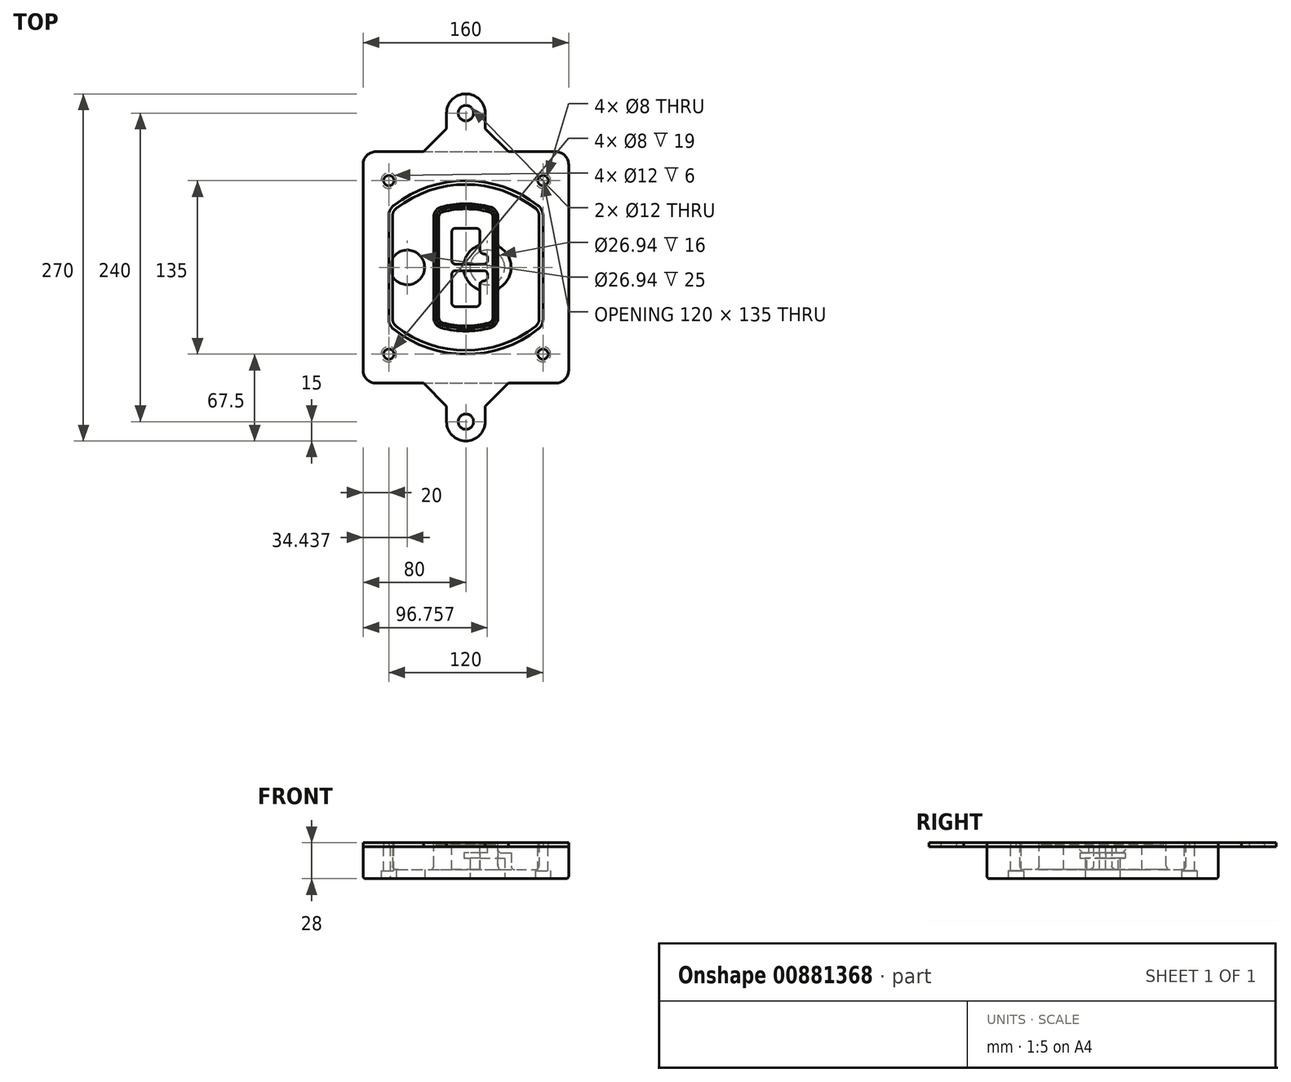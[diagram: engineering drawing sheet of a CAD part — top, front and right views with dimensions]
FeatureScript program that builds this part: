
annotation { "Feature Type Name" : "Feature", "Feature Type Description" : "" }
export const myFeature = defineFeature(function(context is Context, id is Id, definition is map)
    precondition{}
    {
        {
            var Q0;
            Q0=qCreatedBy(makeId("Top.planeOp"),FACE);
            var sketch = newSketch(context, id + "F0", { "sketchPlane" : qUnion([Q0])});
            skPoint(sketch, "E0.rect.middle", {"position": v(0, 0) * mm});
            skLineSegment(sketch, "E1.bottom", {"start": v(-70, -90) * mm, "end": v(70, -90) * mm});
            skLineSegment(sketch, "E1.top", {"start": v(-70, 90) * mm, "end": v(70, 90) * mm});
            skLineSegment(sketch, "E1.left", {"start": v(-80, -80) * mm, "end": v(-80, 80) * mm});
            skLineSegment(sketch, "E1.right", {"start": v(80, -80) * mm, "end": v(80, 80) * mm});
            skLineSegment(sketch, "E2", {"start": v(-80, 90) * mm, "end": v(80, -90) * mm, "construction": true});
            skLineSegment(sketch, "E3", {"start": v(80, 90) * mm, "end": v(-80, -90) * mm, "construction": true});
            skCircle(sketch, "E4", {"center": v(-60, 67.5) * mm, "radius": 4 * mm});
            skCircle(sketch, "E5", {"center": v(60, 67.5) * mm, "radius": 4 * mm});
            skCircle(sketch, "E6", {"center": v(60, -67.5) * mm, "radius": 4 * mm});
            skCircle(sketch, "E7", {"center": v(-60, -67.5) * mm, "radius": 4 * mm});
            skLineSegment(sketch, "E8", {"start": v(-60, 67.5) * mm, "end": v(60, 67.5) * mm, "construction": true});
            skLineSegment(sketch, "E9", {"start": v(60, 67.5) * mm, "end": v(60, -67.5) * mm, "construction": true});
            skLineSegment(sketch, "E10", {"start": v(60, -67.5) * mm, "end": v(-60, -67.5) * mm, "construction": true});
            skLineSegment(sketch, "E11", {"start": v(-60, -67.5) * mm, "end": v(-60, 67.5) * mm, "construction": true});
            skLineSegment(sketch, "E12", {"start": v(-60, 40.3) * mm, "end": v(-60, -40.3) * mm});
            skLineSegment(sketch, "E13", {"start": v(60, 40.3) * mm, "end": v(60, -40.3) * mm});
            skArc(sketch, "E14", {"start": v(56.15, 48.18) * mm, "mid": v(0, 67.5) * mm, "end": v(-56.15, 48.18) * mm});
            skArc(sketch, "E15", {"start": v(-56.15, -48.18) * mm, "mid": v(0, -67.5) * mm, "end": v(56.15, -48.18) * mm});
            skLineSegment(sketch, "E16", {"start": v(-60, 0) * mm, "end": v(60, 0) * mm, "construction": true});
            skPoint(sketch, "E17.visualSharp", {"position": v(-60, -45) * mm});
            skArc(sketch, "E17.filletArc", {"start": v(-60, -40.3) * mm, "mid": v(-58.99, -44.68) * mm, "end": v(-56.15, -48.18) * mm});
            skPoint(sketch, "E18.visualSharp", {"position": v(-60, 45) * mm});
            skArc(sketch, "E18.filletArc", {"start": v(-56.15, 48.18) * mm, "mid": v(-58.99, 44.68) * mm, "end": v(-60, 40.3) * mm});
            skPoint(sketch, "E19.visualSharp", {"position": v(60, 45) * mm});
            skArc(sketch, "E19.filletArc", {"start": v(60, 40.3) * mm, "mid": v(58.99, 44.68) * mm, "end": v(56.15, 48.18) * mm});
            skPoint(sketch, "E20.visualSharp", {"position": v(60, -45) * mm});
            skArc(sketch, "E20.filletArc", {"start": v(56.15, -48.18) * mm, "mid": v(58.99, -44.68) * mm, "end": v(60, -40.3) * mm});
            skPoint(sketch, "E21.visualSharp", {"position": v(-80, 90) * mm});
            skArc(sketch, "E21.filletArc", {"start": v(-70, 90) * mm, "mid": v(-77.07, 87.07) * mm, "end": v(-80, 80) * mm});
            skPoint(sketch, "E22.visualSharp", {"position": v(80, 90) * mm});
            skArc(sketch, "E22.filletArc", {"start": v(80, 80) * mm, "mid": v(77.07, 87.07) * mm, "end": v(70, 90) * mm});
            skPoint(sketch, "E23.visualSharp", {"position": v(80, -90) * mm});
            skArc(sketch, "E23.filletArc", {"start": v(70, -90) * mm, "mid": v(77.07, -87.07) * mm, "end": v(80, -80) * mm});
            skPoint(sketch, "E24.visualSharp", {"position": v(-80, -90) * mm});
            skArc(sketch, "E24.filletArc", {"start": v(-80, -80) * mm, "mid": v(-77.07, -87.07) * mm, "end": v(-70, -90) * mm});
            skArc(sketch, "E25.0", {"start": v(57, 40.3) * mm, "mid": v(56.3, 43.36) * mm, "end": v(54.3, 45.81) * mm});
            skLineSegment(sketch, "E25.1", {"start": v(57, 40.3) * mm, "end": v(57, -40.3) * mm});
            skArc(sketch, "E25.2", {"start": v(54.3, -45.81) * mm, "mid": v(56.3, -43.36) * mm, "end": v(57, -40.3) * mm});
            skArc(sketch, "E25.3", {"start": v(-54.3, -45.81) * mm, "mid": v(0, -64.5) * mm, "end": v(54.3, -45.81) * mm});
            skArc(sketch, "E25.4", {"start": v(-57, -40.3) * mm, "mid": v(-56.3, -43.36) * mm, "end": v(-54.3, -45.81) * mm});
            skArc(sketch, "E25.5", {"start": v(54.3, 45.81) * mm, "mid": v(0, 64.5) * mm, "end": v(-54.3, 45.81) * mm});
            skLineSegment(sketch, "E25.6", {"start": v(-57, 40.3) * mm, "end": v(-57, -40.3) * mm});
            skArc(sketch, "E25.7", {"start": v(-54.3, 45.81) * mm, "mid": v(-56.3, 43.36) * mm, "end": v(-57, 40.3) * mm});
            skArc(sketch, "E26.0", {"start": v(-58.62, 51.33) * mm, "mid": v(-62.58, 46.43) * mm, "end": v(-64, 40.3) * mm});
            skArc(sketch, "E26.1", {"start": v(58.62, 51.33) * mm, "mid": v(0, 71.5) * mm, "end": v(-58.62, 51.33) * mm});
            skArc(sketch, "E26.2", {"start": v(64, 40.3) * mm, "mid": v(62.58, 46.43) * mm, "end": v(58.62, 51.33) * mm});
            skLineSegment(sketch, "E26.3", {"start": v(64, 40.3) * mm, "end": v(64, -40.3) * mm});
            skArc(sketch, "E26.4", {"start": v(58.62, -51.33) * mm, "mid": v(62.58, -46.43) * mm, "end": v(64, -40.3) * mm});
            skLineSegment(sketch, "E26.5", {"start": v(-64, 40.3) * mm, "end": v(-64, -40.3) * mm});
            skArc(sketch, "E26.6", {"start": v(-58.62, -51.33) * mm, "mid": v(0, -71.5) * mm, "end": v(58.62, -51.33) * mm});
            skArc(sketch, "E26.7", {"start": v(-64, -40.3) * mm, "mid": v(-62.58, -46.43) * mm, "end": v(-58.62, -51.33) * mm});
            skSolve(sketch);
        }
        {
            var Q0;
            Q0=makeQuery(id+"F0.imprint","IMPRINT",FACE,{"disambiguationData":[TD([[makeQuery(id+"F0.imprint","IMPRINT",EDGE,{"derivedFrom":sQuery(id+"F0.wireOp",EDGE,"E1.bottom")}),1.0]])]});
            var Q1;
            Q1=makeQuery(id+"F0.imprint","IMPRINT",FACE,{"disambiguationData":[TD([[makeQuery(id+"F0.imprint","IMPRINT",EDGE,{"derivedFrom":sQuery(id+"F0.wireOp",EDGE,"E12")}),1.0]])]});
            var Q2;
            Q2=makeQuery(id+"F0.imprint","IMPRINT",FACE,{"disambiguationData":[TD([[makeQuery(id+"F0.imprint","IMPRINT",EDGE,{"derivedFrom":sQuery(id+"F0.wireOp",EDGE,"E25.0")}),1.0]])]});
            var Q3;
            Q3=makeQuery(id+"F0.imprint","IMPRINT",FACE,{"disambiguationData":[TD([[makeQuery(id+"F0.imprint","IMPRINT",EDGE,{"derivedFrom":sQuery(id+"F0.wireOp",EDGE,"E12")}),-1.0]])]});
            extrude(context, id + "F1", {"entities" : qUnion([Q0, Q1, Q2, Q3]), "oppositeDirection" : true, "depth" : 25 * mm});
        }
        {
            var Q0;
            Q0=makeQuery(id+"F0.imprint","IMPRINT",FACE,{"disambiguationData":[TD([[makeQuery(id+"F0.imprint","IMPRINT",EDGE,{"derivedFrom":sQuery(id+"F0.wireOp",EDGE,"E12")}),1.0]])]});
            extrude(context, id + "F2", {"entities" : qUnion([Q0]), "operationType" : NewBodyOperationType.ADD, "depth" : 3 * mm});
        }
        {
            var Q0;
            Q0=makeQuery(id+"F0.imprint","IMPRINT",FACE,{"disambiguationData":[TD([[makeQuery(id+"F0.imprint","IMPRINT",EDGE,{"derivedFrom":sQuery(id+"F0.wireOp",EDGE,"E25.0")}),1.0]])]});
            extrude(context, id + "F3", {"entities" : qUnion([Q0]), "operationType" : NewBodyOperationType.REMOVE, "oppositeDirection" : true, "depth" : 18 * mm});
        }
        {
            var Q0;
            Q0=makeQuery(id+"F2.opExtrude","CAP_FACE",FACE,{"disambiguationData":[OSD([sQuery(id+"F0.wireOp",EDGE,"E12"),sQuery(id+"F0.wireOp",EDGE,"E13"),sQuery(id+"F0.wireOp",EDGE,"E14"),sQuery(id+"F0.wireOp",EDGE,"E15"),sQuery(id+"F0.wireOp",EDGE,"E17.filletArc"),sQuery(id+"F0.wireOp",EDGE,"E18.filletArc"),sQuery(id+"F0.wireOp",EDGE,"E19.filletArc"),sQuery(id+"F0.wireOp",EDGE,"E20.filletArc"),sQuery(id+"F0.wireOp",EDGE,"E25.0"),sQuery(id+"F0.wireOp",EDGE,"E25.1"),sQuery(id+"F0.wireOp",EDGE,"E25.2"),sQuery(id+"F0.wireOp",EDGE,"E25.3"),sQuery(id+"F0.wireOp",EDGE,"E25.4"),sQuery(id+"F0.wireOp",EDGE,"E25.5"),sQuery(id+"F0.wireOp",EDGE,"E25.6"),sQuery(id+"F0.wireOp",EDGE,"E25.7")])],"isStart":false});
            var sketch = newSketch(context, id + "F4", { "sketchPlane" : qUnion([Q0])});
            skArc(sketch, "E27.0", {"start": v(-19.08, -46.97) * mm, "mid": v(0, -49.5) * mm, "end": v(19.08, -46.97) * mm});
            skArc(sketch, "E28.0", {"start": v(19.08, 46.97) * mm, "mid": v(0, 49.5) * mm, "end": v(-19.08, 46.97) * mm});
            skLineSegment(sketch, "E29", {"start": v(-25, 39.25) * mm, "end": v(-25, -39.25) * mm});
            skLineSegment(sketch, "E30", {"start": v(25, 39.25) * mm, "end": v(25, -39.25) * mm});
            skLineSegment(sketch, "E31", {"start": v(-25, 45.1) * mm, "end": v(25, 45.1) * mm, "construction": true});
            skLineSegment(sketch, "E32", {"start": v(-25, -45.1) * mm, "end": v(25, -45.1) * mm, "construction": true});
            skPoint(sketch, "E33.visualSharp", {"position": v(-25, 45.1) * mm});
            skArc(sketch, "E33.filletArc", {"start": v(-19.08, 46.97) * mm, "mid": v(-23.35, 44.11) * mm, "end": v(-25, 39.25) * mm});
            skPoint(sketch, "E34.visualSharp", {"position": v(25, 45.1) * mm});
            skArc(sketch, "E34.filletArc", {"start": v(25, 39.25) * mm, "mid": v(23.35, 44.11) * mm, "end": v(19.08, 46.97) * mm});
            skPoint(sketch, "E35.visualSharp", {"position": v(25, -45.1) * mm});
            skArc(sketch, "E35.filletArc", {"start": v(19.08, -46.97) * mm, "mid": v(23.35, -44.11) * mm, "end": v(25, -39.25) * mm});
            skPoint(sketch, "E36.visualSharp", {"position": v(-25, -45.1) * mm});
            skArc(sketch, "E36.filletArc", {"start": v(-25, -39.25) * mm, "mid": v(-23.35, -44.11) * mm, "end": v(-19.08, -46.97) * mm});
            skArc(sketch, "E37.0", {"start": v(54.3, 45.81) * mm, "mid": v(0, 64.5) * mm, "end": v(-54.3, 45.81) * mm});
            skArc(sketch, "E37.1", {"start": v(-54.3, 45.81) * mm, "mid": v(-56.3, 43.36) * mm, "end": v(-57, 40.3) * mm});
            skLineSegment(sketch, "E37.2", {"start": v(-57, 40.3) * mm, "end": v(-57, -40.3) * mm});
            skArc(sketch, "E37.3", {"start": v(-57, -40.3) * mm, "mid": v(-56.3, -43.36) * mm, "end": v(-54.3, -45.81) * mm});
            skArc(sketch, "E37.4", {"start": v(-54.3, -45.81) * mm, "mid": v(0, -64.5) * mm, "end": v(54.3, -45.81) * mm});
            skArc(sketch, "E37.5", {"start": v(54.3, -45.81) * mm, "mid": v(56.3, -43.36) * mm, "end": v(57, -40.3) * mm});
            skLineSegment(sketch, "E37.6", {"start": v(57, 40.3) * mm, "end": v(57, -40.3) * mm});
            skArc(sketch, "E37.7", {"start": v(57, 40.3) * mm, "mid": v(56.3, 43.36) * mm, "end": v(54.3, 45.81) * mm});
            skLineSegment(sketch, "E38.0", {"start": v(23, 39.25) * mm, "end": v(23, -39.25) * mm});
            skArc(sketch, "E38.1", {"start": v(18.56, -45.04) * mm, "mid": v(21.76, -42.9) * mm, "end": v(23, -39.25) * mm});
            skArc(sketch, "E38.2", {"start": v(-18.56, -45.04) * mm, "mid": v(0, -47.5) * mm, "end": v(18.56, -45.04) * mm});
            skArc(sketch, "E38.3", {"start": v(-23, -39.25) * mm, "mid": v(-21.76, -42.9) * mm, "end": v(-18.56, -45.04) * mm});
            skLineSegment(sketch, "E38.4", {"start": v(-23, 39.25) * mm, "end": v(-23, -39.25) * mm});
            skArc(sketch, "E38.5", {"start": v(23, 39.25) * mm, "mid": v(21.76, 42.9) * mm, "end": v(18.56, 45.04) * mm});
            skArc(sketch, "E38.6", {"start": v(-18.56, 45.04) * mm, "mid": v(-21.76, 42.9) * mm, "end": v(-23, 39.25) * mm});
            skArc(sketch, "E38.7", {"start": v(18.56, 45.04) * mm, "mid": v(0, 47.5) * mm, "end": v(-18.56, 45.04) * mm});
            skArc(sketch, "E39.0", {"start": v(21, 39.25) * mm, "mid": v(20.18, 41.68) * mm, "end": v(18.04, 43.1) * mm});
            skLineSegment(sketch, "E39.1", {"start": v(21, 39.25) * mm, "end": v(21, -39.25) * mm});
            skArc(sketch, "E39.2", {"start": v(18.04, -43.1) * mm, "mid": v(20.18, -41.68) * mm, "end": v(21, -39.25) * mm});
            skArc(sketch, "E39.3", {"start": v(-18.04, -43.1) * mm, "mid": v(0, -45.5) * mm, "end": v(18.04, -43.1) * mm});
            skArc(sketch, "E39.4", {"start": v(-21, -39.25) * mm, "mid": v(-20.18, -41.68) * mm, "end": v(-18.04, -43.1) * mm});
            skArc(sketch, "E39.5", {"start": v(18.04, 43.1) * mm, "mid": v(0, 45.5) * mm, "end": v(-18.04, 43.1) * mm});
            skLineSegment(sketch, "E39.6", {"start": v(-21, 39.25) * mm, "end": v(-21, -39.25) * mm});
            skArc(sketch, "E39.7", {"start": v(-18.04, 43.1) * mm, "mid": v(-20.18, 41.68) * mm, "end": v(-21, 39.25) * mm});
            skLineSegment(sketch, "E40", {"start": v(-25, 0) * mm, "end": v(25, 0) * mm, "construction": true});
            skLineSegment(sketch, "E41", {"start": v(-11, 5.5) * mm, "end": v(-11, 27.5) * mm});
            skLineSegment(sketch, "E42", {"start": v(-8, 30.5) * mm, "end": v(8, 30.5) * mm});
            skLineSegment(sketch, "E43", {"start": v(11, 27.5) * mm, "end": v(11, 13.5) * mm});
            skLineSegment(sketch, "E44", {"start": v(14, 10.5) * mm, "end": v(14, 10.5) * mm});
            skLineSegment(sketch, "E45", {"start": v(17, 7.5) * mm, "end": v(17, 5.5) * mm});
            skLineSegment(sketch, "E46", {"start": v(14, 2.5) * mm, "end": v(-8, 2.5) * mm});
            skPoint(sketch, "E47.visualSharp", {"position": v(-11, 30.5) * mm});
            skArc(sketch, "E47.filletArc", {"start": v(-8, 30.5) * mm, "mid": v(-10.12, 29.62) * mm, "end": v(-11, 27.5) * mm});
            skPoint(sketch, "E48.visualSharp", {"position": v(11, 30.5) * mm});
            skArc(sketch, "E48.filletArc", {"start": v(11, 27.5) * mm, "mid": v(10.12, 29.62) * mm, "end": v(8, 30.5) * mm});
            skPoint(sketch, "E49.visualSharp", {"position": v(11, 10.5) * mm});
            skArc(sketch, "E49.filletArc", {"start": v(11, 13.5) * mm, "mid": v(11.88, 11.38) * mm, "end": v(14, 10.5) * mm});
            skPoint(sketch, "E50.visualSharp", {"position": v(17, 10.5) * mm});
            skArc(sketch, "E50.filletArc", {"start": v(17, 7.5) * mm, "mid": v(16.12, 9.62) * mm, "end": v(14, 10.5) * mm});
            skPoint(sketch, "E51.visualSharp", {"position": v(17, 2.5) * mm});
            skArc(sketch, "E51.filletArc", {"start": v(14, 2.5) * mm, "mid": v(16.12, 3.38) * mm, "end": v(17, 5.5) * mm});
            skPoint(sketch, "E52.visualSharp", {"position": v(-11, 2.5) * mm});
            skArc(sketch, "E52.filletArc", {"start": v(-11, 5.5) * mm, "mid": v(-10.12, 3.38) * mm, "end": v(-8, 2.5) * mm});
            skLineSegment(sketch, "E53.0.MirrorCS", {"start": v(14, -2.5) * mm, "end": v(-8, -2.5) * mm});
            skArc(sketch, "E54.0.MirrorCS", {"start": v(-11, -5.5) * mm, "mid": v(-10.12, -3.38) * mm, "end": v(-8, -2.5) * mm});
            skLineSegment(sketch, "E55.0.MirrorCS", {"start": v(-11, -5.5) * mm, "end": v(-11, -27.5) * mm});
            skArc(sketch, "E56.0.MirrorCS", {"start": v(-8, -30.5) * mm, "mid": v(-10.12, -29.62) * mm, "end": v(-11, -27.5) * mm});
            skLineSegment(sketch, "E57.0.MirrorCS", {"start": v(-8, -30.5) * mm, "end": v(8, -30.5) * mm});
            skArc(sketch, "E58.0.MirrorCS", {"start": v(11, -27.5) * mm, "mid": v(10.12, -29.62) * mm, "end": v(8, -30.5) * mm});
            skLineSegment(sketch, "E59.0.MirrorCS", {"start": v(11, -27.5) * mm, "end": v(11, -13.5) * mm});
            skArc(sketch, "E60.0.MirrorCS", {"start": v(11, -13.5) * mm, "mid": v(11.88, -11.38) * mm, "end": v(14, -10.5) * mm});
            skArc(sketch, "E61.0.MirrorCS", {"start": v(17, -7.5) * mm, "mid": v(16.12, -9.62) * mm, "end": v(14, -10.5) * mm});
            skLineSegment(sketch, "E62.0.MirrorCS", {"start": v(17, -7.5) * mm, "end": v(17, -5.5) * mm});
            skArc(sketch, "E63.0.MirrorCS", {"start": v(14, -2.5) * mm, "mid": v(16.12, -3.38) * mm, "end": v(17, -5.5) * mm});
            skSolve(sketch);
        }
        {
            var Q0;
            Q0=makeQuery(id+"F4.imprint","IMPRINT",FACE,{"disambiguationData":[TD([[makeQuery(id+"F4.imprint","IMPRINT",EDGE,{"derivedFrom":sQuery(id+"F4.wireOp",EDGE,"E27.0")}),1.0]])]});
            var Q1;
            Q1=makeQuery(id+"F4.imprint","IMPRINT",FACE,{"disambiguationData":[TD([[makeQuery(id+"F4.imprint","IMPRINT",EDGE,{"derivedFrom":sQuery(id+"F4.wireOp",EDGE,"E38.0")}),-1.0]])]});
            var Q2;
            Q2=makeQuery(id+"F4.imprint","IMPRINT",FACE,{"disambiguationData":[TD([[makeQuery(id+"F4.imprint","IMPRINT",EDGE,{"derivedFrom":sQuery(id+"F4.wireOp",EDGE,"E39.0")}),1.0]])]});
            extrude(context, id + "F5", {"entities" : qUnion([Q0, Q1, Q2]), "operationType" : NewBodyOperationType.ADD, "endBound" : BoundingType.UP_TO_NEXT, "oppositeDirection" : true, "depth" : 25 * mm});
        }
        {
            var Q0;
            Q0=makeQuery(id+"F4.imprint","IMPRINT",FACE,{"disambiguationData":[TD([[makeQuery(id+"F4.imprint","IMPRINT",EDGE,{"derivedFrom":sQuery(id+"F4.wireOp",EDGE,"E38.0")}),-1.0]])]});
            extrude(context, id + "F6", {"entities" : qUnion([Q0]), "operationType" : NewBodyOperationType.REMOVE, "oppositeDirection" : true, "depth" : 2 * mm});
        }
        {
            var Q0;
            Q0=makeQuery(id+"F1.opExtrude","CAP_FACE",FACE,{"disambiguationData":[OSD([sQuery(id+"F0.wireOp",EDGE,"E1.bottom"),sQuery(id+"F0.wireOp",EDGE,"E1.top"),sQuery(id+"F0.wireOp",EDGE,"E1.left"),sQuery(id+"F0.wireOp",EDGE,"E1.right"),sQuery(id+"F0.wireOp",EDGE,"E4"),sQuery(id+"F0.wireOp",EDGE,"E5"),sQuery(id+"F0.wireOp",EDGE,"E6"),sQuery(id+"F0.wireOp",EDGE,"E7"),sQuery(id+"F0.wireOp",EDGE,"E21.filletArc"),sQuery(id+"F0.wireOp",EDGE,"E22.filletArc"),sQuery(id+"F0.wireOp",EDGE,"E23.filletArc"),sQuery(id+"F0.wireOp",EDGE,"E24.filletArc")])],"isStart":false});
            var sketch = newSketch(context, id + "F7", { "sketchPlane" : qUnion([Q0])});
            skCircle(sketch, "E64", {"center": v(16.76, 0) * mm, "radius": 13.47 * mm});
            skCircle(sketch, "E65", {"center": v(-45.56, 0) * mm, "radius": 13.47 * mm});
            skLineSegment(sketch, "E66", {"start": v(80, 0) * mm, "end": v(-80, 0) * mm});
            skCircle(sketch, "E67", {"center": v(16.76, 0) * mm, "radius": 18.47 * mm});
            skCircle(sketch, "E68", {"center": v(60, -67.5) * mm, "radius": 6 * mm});
            skCircle(sketch, "E69", {"center": v(-60, -67.5) * mm, "radius": 6 * mm});
            skCircle(sketch, "E70", {"center": v(-60, 67.5) * mm, "radius": 6 * mm});
            skCircle(sketch, "E71", {"center": v(60, 67.5) * mm, "radius": 6 * mm});
            skSolve(sketch);
        }
        {
            var Q0;
            {var subQ1=sQuery(id+"F7.wireOp",EDGE,"E66");var subQ4=sQuery(id+"F7.wireOp",EDGE,"E64");var subQ6=makeQuery(id+"F7.imprint","INTERSECT",VERTEX,{"disambiguationData":[OD(0.0)],"derivedFrom":[subQ4,subQ1]});Q0=makeQuery(id+"F7.imprint","IMPRINT",FACE,{"disambiguationData":[TD([[makeQuery(id+"F7.imprint","IMPRINT",EDGE,{"disambiguationData":[TD([[subQ6,-1.0]])],"derivedFrom":subQ4}),-1.0]])]});}
            var Q1;
            {var subQ0=sQuery(id+"F7.wireOp",EDGE,"E66");var subQ1=sQuery(id+"F7.wireOp",EDGE,"E64");var subQ3=makeQuery(id+"F7.imprint","INTERSECT",VERTEX,{"disambiguationData":[OD(0.0)],"derivedFrom":[subQ1,subQ0]});Q1=makeQuery(id+"F7.imprint","IMPRINT",FACE,{"disambiguationData":[TD([[makeQuery(id+"F7.imprint","IMPRINT",EDGE,{"disambiguationData":[TD([[subQ3,-1.0]])],"derivedFrom":subQ1}),1.0]])]});}
            var Q2;
            {var subQ0=sQuery(id+"F7.wireOp",EDGE,"E66");var subQ1=sQuery(id+"F7.wireOp",EDGE,"E64");var subQ3=makeQuery(id+"F7.imprint","INTERSECT",VERTEX,{"disambiguationData":[OD(0.0)],"derivedFrom":[subQ1,subQ0]});Q2=makeQuery(id+"F7.imprint","IMPRINT",FACE,{"disambiguationData":[TD([[makeQuery(id+"F7.imprint","IMPRINT",EDGE,{"disambiguationData":[TD([[subQ3,1.0]])],"derivedFrom":subQ1}),1.0]])]});}
            var Q3;
            {var subQ1=sQuery(id+"F7.wireOp",EDGE,"E66");var subQ4=sQuery(id+"F7.wireOp",EDGE,"E64");var subQ6=makeQuery(id+"F7.imprint","INTERSECT",VERTEX,{"disambiguationData":[OD(0.0)],"derivedFrom":[subQ4,subQ1]});Q3=makeQuery(id+"F7.imprint","IMPRINT",FACE,{"disambiguationData":[TD([[makeQuery(id+"F7.imprint","IMPRINT",EDGE,{"disambiguationData":[TD([[subQ6,1.0]])],"derivedFrom":subQ4}),-1.0]])]});}
            extrude(context, id + "F8", {"entities" : qUnion([Q0, Q1, Q2, Q3]), "operationType" : NewBodyOperationType.ADD, "oppositeDirection" : true, "depth" : 20 * mm});
        }
        {
            var Q0;
            {var subQ0=sQuery(id+"F7.wireOp",EDGE,"E66");var subQ1=sQuery(id+"F7.wireOp",EDGE,"E64");var subQ3=makeQuery(id+"F7.imprint","INTERSECT",VERTEX,{"disambiguationData":[OD(0.0)],"derivedFrom":[subQ1,subQ0]});Q0=makeQuery(id+"F7.imprint","IMPRINT",FACE,{"disambiguationData":[TD([[makeQuery(id+"F7.imprint","IMPRINT",EDGE,{"disambiguationData":[TD([[subQ3,-1.0]])],"derivedFrom":subQ1}),1.0]])]});}
            var Q1;
            {var subQ0=sQuery(id+"F7.wireOp",EDGE,"E66");var subQ1=sQuery(id+"F7.wireOp",EDGE,"E64");var subQ3=makeQuery(id+"F7.imprint","INTERSECT",VERTEX,{"disambiguationData":[OD(0.0)],"derivedFrom":[subQ1,subQ0]});Q1=makeQuery(id+"F7.imprint","IMPRINT",FACE,{"disambiguationData":[TD([[makeQuery(id+"F7.imprint","IMPRINT",EDGE,{"disambiguationData":[TD([[subQ3,1.0]])],"derivedFrom":subQ1}),1.0]])]});}
            extrude(context, id + "F9", {"entities" : qUnion([Q0, Q1]), "operationType" : NewBodyOperationType.REMOVE, "oppositeDirection" : true, "depth" : 16 * mm});
        }
        {
            var Q0;
            {var subQ0=sQuery(id+"F7.wireOp",EDGE,"E66");var subQ1=sQuery(id+"F7.wireOp",EDGE,"E65");var subQ3=makeQuery(id+"F7.imprint","INTERSECT",VERTEX,{"disambiguationData":[OD(0.0)],"derivedFrom":[subQ1,subQ0]});Q0=makeQuery(id+"F7.imprint","IMPRINT",FACE,{"disambiguationData":[TD([[makeQuery(id+"F7.imprint","IMPRINT",EDGE,{"disambiguationData":[TD([[subQ3,-1.0]])],"derivedFrom":subQ1}),1.0]])]});}
            var Q1;
            {var subQ0=sQuery(id+"F7.wireOp",EDGE,"E66");var subQ1=sQuery(id+"F7.wireOp",EDGE,"E65");var subQ3=makeQuery(id+"F7.imprint","INTERSECT",VERTEX,{"disambiguationData":[OD(0.0)],"derivedFrom":[subQ1,subQ0]});Q1=makeQuery(id+"F7.imprint","IMPRINT",FACE,{"disambiguationData":[TD([[makeQuery(id+"F7.imprint","IMPRINT",EDGE,{"disambiguationData":[TD([[subQ3,1.0]])],"derivedFrom":subQ1}),1.0]])]});}
            extrude(context, id + "F10", {"entities" : qUnion([Q0, Q1]), "operationType" : NewBodyOperationType.REMOVE, "oppositeDirection" : true, "depth" : 25 * mm});
        }
        {
            var Q0;
            Q0=makeQuery(id+"F7.imprint","IMPRINT",FACE,{"disambiguationData":[TD([[makeQuery(id+"F7.imprint","IMPRINT",EDGE,{"derivedFrom":sQuery(id+"F7.wireOp",EDGE,"E68")}),1.0]])]});
            var Q1;
            Q1=makeQuery(id+"F7.imprint","IMPRINT",FACE,{"disambiguationData":[TD([[makeQuery(id+"F7.imprint","IMPRINT",EDGE,{"derivedFrom":makeQuery(id+"F1.opExtrude","CAP_EDGE",EDGE,{"disambiguationData":[OSD([sQuery(id+"F0.wireOp",EDGE,"E5")])],"isStart":false})}),-1.0]])]});
            var Q2;
            Q2=makeQuery(id+"F7.imprint","IMPRINT",FACE,{"disambiguationData":[TD([[makeQuery(id+"F7.imprint","IMPRINT",EDGE,{"derivedFrom":sQuery(id+"F7.wireOp",EDGE,"E69")}),1.0]])]});
            var Q3;
            Q3=makeQuery(id+"F7.imprint","IMPRINT",FACE,{"disambiguationData":[TD([[makeQuery(id+"F7.imprint","IMPRINT",EDGE,{"derivedFrom":makeQuery(id+"F1.opExtrude","CAP_EDGE",EDGE,{"disambiguationData":[OSD([sQuery(id+"F0.wireOp",EDGE,"E4")])],"isStart":false})}),-1.0]])]});
            var Q4;
            Q4=makeQuery(id+"F7.imprint","IMPRINT",FACE,{"disambiguationData":[TD([[makeQuery(id+"F7.imprint","IMPRINT",EDGE,{"derivedFrom":sQuery(id+"F7.wireOp",EDGE,"E70")}),1.0]])]});
            var Q5;
            Q5=makeQuery(id+"F7.imprint","IMPRINT",FACE,{"disambiguationData":[TD([[makeQuery(id+"F7.imprint","IMPRINT",EDGE,{"derivedFrom":makeQuery(id+"F1.opExtrude","CAP_EDGE",EDGE,{"disambiguationData":[OSD([sQuery(id+"F0.wireOp",EDGE,"E7")])],"isStart":false})}),-1.0]])]});
            var Q6;
            Q6=makeQuery(id+"F7.imprint","IMPRINT",FACE,{"disambiguationData":[TD([[makeQuery(id+"F7.imprint","IMPRINT",EDGE,{"derivedFrom":sQuery(id+"F7.wireOp",EDGE,"E71")}),1.0]])]});
            var Q7;
            Q7=makeQuery(id+"F7.imprint","IMPRINT",FACE,{"disambiguationData":[TD([[makeQuery(id+"F7.imprint","IMPRINT",EDGE,{"derivedFrom":makeQuery(id+"F1.opExtrude","CAP_EDGE",EDGE,{"disambiguationData":[OSD([sQuery(id+"F0.wireOp",EDGE,"E6")])],"isStart":false})}),-1.0]])]});
            extrude(context, id + "F11", {"entities" : qUnion([Q0, Q1, Q2, Q3, Q4, Q5, Q6, Q7]), "operationType" : NewBodyOperationType.REMOVE, "oppositeDirection" : true, "depth" : 6 * mm});
        }
        {
            var Q0;
            Q0=makeQuery(id+"F9.boolean.opBoolean","COPY",FACE,{"derivedFrom":makeQuery(id+"F9.opExtrude","CAP_FACE",FACE,{"disambiguationData":[OSD([sQuery(id+"F7.wireOp",EDGE,"E64")])],"isStart":false})});
            var sketch = newSketch(context, id + "F12", { "sketchPlane" : qUnion([Q0])});
            skArc(sketch, "E72.0", {"start": v(11, 17.55) * mm, "mid": v(2.57, 11.82) * mm, "end": v(-1.54, 2.5) * mm});
            skArc(sketch, "E72.1", {"start": v(-1.54, -2.5) * mm, "mid": v(2.57, -11.82) * mm, "end": v(11, -17.55) * mm});
            skLineSegment(sketch, "E73", {"start": v(-1.54, -2.5) * mm, "end": v(14, -2.5) * mm});
            skLineSegment(sketch, "E74.0", {"start": v(14, 2.5) * mm, "end": v(-1.54, 2.5) * mm});
            skArc(sketch, "E74.1", {"start": v(14, 2.5) * mm, "mid": v(16.12, 3.38) * mm, "end": v(17, 5.5) * mm});
            skLineSegment(sketch, "E74.2", {"start": v(17, 7.5) * mm, "end": v(17, 5.5) * mm});
            skArc(sketch, "E74.3", {"start": v(17, 7.5) * mm, "mid": v(16.12, 9.62) * mm, "end": v(14, 10.5) * mm});
            skArc(sketch, "E74.4", {"start": v(11, 13.5) * mm, "mid": v(11.88, 11.38) * mm, "end": v(14, 10.5) * mm});
            skLineSegment(sketch, "E74.5", {"start": v(11, 17.55) * mm, "end": v(11, 13.5) * mm});
            skLineSegment(sketch, "E74.7", {"start": v(14, -2.5) * mm, "end": v(-1.54, -2.5) * mm});
            skArc(sketch, "E74.8", {"start": v(14, -2.5) * mm, "mid": v(16.12, -3.38) * mm, "end": v(17, -5.5) * mm});
            skLineSegment(sketch, "E74.9", {"start": v(17, -7.5) * mm, "end": v(17, -5.5) * mm});
            skArc(sketch, "E74.10", {"start": v(17, -7.5) * mm, "mid": v(16.12, -9.62) * mm, "end": v(14, -10.5) * mm});
            skArc(sketch, "E74.11", {"start": v(11, -13.5) * mm, "mid": v(11.88, -11.38) * mm, "end": v(14, -10.5) * mm});
            skLineSegment(sketch, "E74.12", {"start": v(11, -17.55) * mm, "end": v(11, -13.5) * mm});
            skPoint(sketch, "E75.orphan", {"position": v(11, -27.5) * mm});
            skPoint(sketch, "E76.orphan", {"position": v(-8, -2.5) * mm});
            skPoint(sketch, "E77.orphan", {"position": v(-8, 2.5) * mm});
            skPoint(sketch, "E78.orphan", {"position": v(11, 27.5) * mm});
            skSolve(sketch);
        }
        {
            var Q0;
            {var subQ7=sQuery(id+"F12.wireOp",EDGE,"E72.0");var subQ14=sQuery(id+"F12.wireOp",EDGE,"E72.1");var subQ16=sQuery(id+"F12.wireOp",EDGE,"E74.1");var subQ18=sQuery(id+"F12.wireOp",EDGE,"E74.8");Q0=qUnion([makeQuery(id+"F12.imprint","IMPRINT",FACE,{"disambiguationData":[TD([[makeQuery(id+"F12.imprint","IMPRINT",EDGE,{"derivedFrom":subQ7}),1.0]])]}),makeQuery(id+"F12.imprint","IMPRINT",FACE,{"disambiguationData":[TD([[makeQuery(id+"F12.imprint","IMPRINT",EDGE,{"derivedFrom":subQ14}),1.0]])]}),makeQuery(id+"F12.imprint","IMPRINT",FACE,{"disambiguationData":[TD([[makeQuery(id+"F12.imprint","IMPRINT",EDGE,{"derivedFrom":subQ16}),1.0]])]}),makeQuery(id+"F12.imprint","IMPRINT",FACE,{"disambiguationData":[TD([[makeQuery(id+"F12.imprint","IMPRINT",EDGE,{"derivedFrom":subQ18}),-1.0]])]})]);}
            var Q1;
            Q1=makeQuery(id+"F5.boolean.opBoolean","SPLIT",FACE,{"disambiguationData":[TD([makeQuery(id+"F5.opExtrude","SWEPT_FACE",FACE,{"disambiguationData":[OSD([sQuery(id+"F4.wireOp",EDGE,"E41")])]})])],"derivedFrom":makeQuery(id+"F3.boolean.opBoolean","COPY",FACE,{"derivedFrom":makeQuery(id+"F3.opExtrude","CAP_FACE",FACE,{"disambiguationData":[OSD([sQuery(id+"F0.wireOp",EDGE,"E25.0"),sQuery(id+"F0.wireOp",EDGE,"E25.1"),sQuery(id+"F0.wireOp",EDGE,"E25.2"),sQuery(id+"F0.wireOp",EDGE,"E25.3"),sQuery(id+"F0.wireOp",EDGE,"E25.4"),sQuery(id+"F0.wireOp",EDGE,"E25.5"),sQuery(id+"F0.wireOp",EDGE,"E25.6"),sQuery(id+"F0.wireOp",EDGE,"E25.7")])],"isStart":false})})});
            extrude(context, id + "F13", {"entities" : qUnion([Q0]), "operationType" : NewBodyOperationType.REMOVE, "endBound" : BoundingType.UP_TO_SURFACE, "endBoundEntityFace" : qUnion([Q1]), "depth" : 25 * mm});
        }
        {
            var Q0;
            Q0=makeQuery(id+"F3.boolean.opBoolean","COPY",EDGE,{"derivedFrom":makeQuery(id+"F3.opExtrude","CAP_EDGE",EDGE,{"disambiguationData":[OSD([sQuery(id+"F0.wireOp",EDGE,"E25.6")])],"isStart":false})});
            var Q1;
            Q1=makeQuery(id+"F8.boolean.opBoolean","INTERSECT",EDGE,{"derivedFrom":[makeQuery(id+"F5.opExtrude","SWEPT_FACE",FACE,{"disambiguationData":[OSD([sQuery(id+"F4.wireOp",EDGE,"E30")])]}),makeQuery(id+"F8.opExtrude","CAP_FACE",FACE,{"disambiguationData":[OSD([sQuery(id+"F7.wireOp",EDGE,"E67")])],"isStart":false})]});
            var Q2;
            Q2=makeQuery(id+"F8.boolean.opBoolean","INTERSECT",EDGE,{"disambiguationData":[OD(1.0)],"derivedFrom":[makeQuery(id+"F5.opExtrude","SWEPT_FACE",FACE,{"disambiguationData":[OSD([sQuery(id+"F4.wireOp",EDGE,"E30")])]}),makeQuery(id+"F8.opExtrude","SWEPT_FACE",FACE,{"disambiguationData":[OSD([sQuery(id+"F7.wireOp",EDGE,"E67")])]})]});
            var Q3;
            {var subQ0=sQuery(id+"F4.wireOp",EDGE,"E30");Q3=makeQuery(id+"F8.boolean.opBoolean","SPLIT",EDGE,{"disambiguationData":[TD([makeQuery(id+"F5.opExtrude","SWEPT_FACE",FACE,{"disambiguationData":[OSD([sQuery(id+"F4.wireOp",EDGE,"E35.filletArc")])]})])],"derivedFrom":makeQuery(id+"F5.opExtrude","CAP_EDGE",EDGE,{"disambiguationData":[OSD([subQ0])],"isStart":false})});}
            var Q4;
            {var subQ0=sQuery(id+"F0.wireOp",EDGE,"E25.7");var subQ1=sQuery(id+"F0.wireOp",EDGE,"E25.1");var subQ2=sQuery(id+"F0.wireOp",EDGE,"E25.6");var subQ3=sQuery(id+"F0.wireOp",EDGE,"E25.5");var subQ4=sQuery(id+"F0.wireOp",EDGE,"E25.4");var subQ5=sQuery(id+"F0.wireOp",EDGE,"E25.0");var subQ6=sQuery(id+"F0.wireOp",EDGE,"E25.2");var subQ7=sQuery(id+"F0.wireOp",EDGE,"E25.3");Q4=makeQuery(id+"F8.boolean.opBoolean","INTERSECT",EDGE,{"derivedFrom":[makeQuery(id+"F5.boolean.opBoolean","SPLIT",FACE,{"disambiguationData":[TD([makeQuery(id+"F2.opExtrude","SWEPT_FACE",FACE,{"disambiguationData":[OSD([subQ5])]})])],"derivedFrom":makeQuery(id+"F3.boolean.opBoolean","COPY",FACE,{"derivedFrom":makeQuery(id+"F3.opExtrude","CAP_FACE",FACE,{"disambiguationData":[OSD([subQ5,subQ1,subQ6,subQ7,subQ4,subQ3,subQ2,subQ0])],"isStart":false})})}),makeQuery(id+"F8.opExtrude","SWEPT_FACE",FACE,{"disambiguationData":[OSD([sQuery(id+"F7.wireOp",EDGE,"E67")])]})]});}
            var Q5;
            Q5=makeQuery(id+"F8.boolean.opBoolean","INTERSECT",EDGE,{"disambiguationData":[OD(0.0)],"derivedFrom":[makeQuery(id+"F5.opExtrude","SWEPT_FACE",FACE,{"disambiguationData":[OSD([sQuery(id+"F4.wireOp",EDGE,"E30")])]}),makeQuery(id+"F8.opExtrude","SWEPT_FACE",FACE,{"disambiguationData":[OSD([sQuery(id+"F7.wireOp",EDGE,"E67")])]})]});
            fillet(context, id + "F14", {"entities" : qUnion([Q0, Q1, Q2, Q3, Q4, Q5]), "radius" : 3 * mm, "tangentPropagation" : true, "allowEdgeOverflow" : false});
        }
        {
            var Q0;
            Q0=makeQuery(id+"F1.opExtrude","CAP_EDGE",EDGE,{"disambiguationData":[OSD([sQuery(id+"F0.wireOp",EDGE,"E1.bottom")])],"isStart":false});
            fillet(context, id + "F15", {"entities" : qUnion([Q0]), "radius" : 2 * mm, "tangentPropagation" : true, "allowEdgeOverflow" : false});
        }
        {
            var Q0;
            {var subQ0=sQuery(id+"F0.wireOp",EDGE,"E21.filletArc");var subQ1=sQuery(id+"F0.wireOp",EDGE,"E7");var subQ2=sQuery(id+"F0.wireOp",EDGE,"E6");var subQ3=sQuery(id+"F0.wireOp",EDGE,"E5");var subQ4=sQuery(id+"F0.wireOp",EDGE,"E4");var subQ5=sQuery(id+"F0.wireOp",EDGE,"E22.filletArc");var subQ6=sQuery(id+"F0.wireOp",EDGE,"E1.bottom");var subQ7=sQuery(id+"F0.wireOp",EDGE,"E1.right");var subQ8=sQuery(id+"F0.wireOp",EDGE,"E1.top");var subQ9=sQuery(id+"F0.wireOp",EDGE,"E1.left");var subQ10=sQuery(id+"F0.wireOp",EDGE,"E23.filletArc");var subQ11=sQuery(id+"F0.wireOp",EDGE,"E24.filletArc");Q0=makeQuery(id+"F2.boolean.opBoolean","SPLIT",FACE,{"disambiguationData":[TD([makeQuery(id+"F1.opExtrude","SWEPT_FACE",FACE,{"disambiguationData":[OSD([subQ6])]})])],"derivedFrom":makeQuery(id+"F1.opExtrude","CAP_FACE",FACE,{"disambiguationData":[OSD([subQ6,subQ8,subQ9,subQ7,subQ4,subQ3,subQ2,subQ1,subQ0,subQ5,subQ10,subQ11])],"isStart":true})});}
            var sketch = newSketch(context, id + "F16", { "sketchPlane" : qUnion([Q0])});
            skLineSegment(sketch, "E79.0", {"start": v(-80, -80) * mm, "end": v(-80, 80) * mm});
            skLineSegment(sketch, "E79.1", {"start": v(-70, 90) * mm, "end": v(70, 90) * mm});
            skCircle(sketch, "E79.2", {"center": v(-60, 67.5) * mm, "radius": 4 * mm});
            skCircle(sketch, "E79.3", {"center": v(60, 67.5) * mm, "radius": 4 * mm});
            skCircle(sketch, "E79.4", {"center": v(60, -67.5) * mm, "radius": 4 * mm});
            skCircle(sketch, "E79.5", {"center": v(-60, -67.5) * mm, "radius": 4 * mm});
            skLineSegment(sketch, "E79.6", {"start": v(80, -80) * mm, "end": v(80, 80) * mm});
            skLineSegment(sketch, "E79.7", {"start": v(-70, -90) * mm, "end": v(70, -90) * mm});
            skArc(sketch, "E79.8", {"start": v(80, 80) * mm, "mid": v(77.07, 87.07) * mm, "end": v(70, 90) * mm});
            skArc(sketch, "E79.9", {"start": v(-70, 90) * mm, "mid": v(-77.07, 87.07) * mm, "end": v(-80, 80) * mm});
            skArc(sketch, "E79.10", {"start": v(-80, -80) * mm, "mid": v(-77.07, -87.07) * mm, "end": v(-70, -90) * mm});
            skArc(sketch, "E79.11", {"start": v(70, -90) * mm, "mid": v(77.07, -87.07) * mm, "end": v(80, -80) * mm});
            skArc(sketch, "E79.12", {"start": v(56.15, 48.18) * mm, "mid": v(0, 67.5) * mm, "end": v(-56.15, 48.18) * mm});
            skArc(sketch, "E79.13", {"start": v(60, 40.3) * mm, "mid": v(58.99, 44.68) * mm, "end": v(56.15, 48.18) * mm});
            skLineSegment(sketch, "E79.14", {"start": v(60, 40.3) * mm, "end": v(60, -40.3) * mm});
            skArc(sketch, "E79.15", {"start": v(56.15, -48.18) * mm, "mid": v(58.99, -44.68) * mm, "end": v(60, -40.3) * mm});
            skArc(sketch, "E79.16", {"start": v(-56.15, -48.18) * mm, "mid": v(0, -67.5) * mm, "end": v(56.15, -48.18) * mm});
            skArc(sketch, "E79.17", {"start": v(-60, -40.3) * mm, "mid": v(-58.99, -44.68) * mm, "end": v(-56.15, -48.18) * mm});
            skLineSegment(sketch, "E79.18", {"start": v(-60, 40.3) * mm, "end": v(-60, -40.3) * mm});
            skArc(sketch, "E79.19", {"start": v(-56.15, 48.18) * mm, "mid": v(-58.99, 44.68) * mm, "end": v(-60, 40.3) * mm});
            skLineSegment(sketch, "E80", {"start": v(-33, 90) * mm, "end": v(-15, 108) * mm});
            skCircle(sketch, "E81", {"center": v(0, 120) * mm, "radius": 6 * mm});
            skLineSegment(sketch, "E82", {"start": v(33, 90) * mm, "end": v(15, 108) * mm});
            skArc(sketch, "E83", {"start": v(15, 120) * mm, "mid": v(0, 135) * mm, "end": v(-15, 120) * mm});
            skLineSegment(sketch, "E84", {"start": v(-15, 120) * mm, "end": v(-15, 108) * mm});
            skLineSegment(sketch, "E85", {"start": v(15, 120) * mm, "end": v(15, 108) * mm});
            skLineSegment(sketch, "E86", {"start": v(-80, 0) * mm, "end": v(80, 0) * mm, "construction": true});
            skArc(sketch, "E87.MirrorCS", {"start": v(15, -120) * mm, "mid": v(0, -135) * mm, "end": v(-15, -120) * mm});
            skCircle(sketch, "E88.MirrorC", {"center": v(0, -120) * mm, "radius": 6 * mm});
            skLineSegment(sketch, "E89.MirrorCS", {"start": v(-33, -90) * mm, "end": v(-15, -108) * mm});
            skLineSegment(sketch, "E90.MirrorCS", {"start": v(-15, -120) * mm, "end": v(-15, -108) * mm});
            skLineSegment(sketch, "E91.MirrorCS", {"start": v(33, -90) * mm, "end": v(15, -108) * mm});
            skLineSegment(sketch, "E92.MirrorCS", {"start": v(15, -120) * mm, "end": v(15, -108) * mm});
            skSolve(sketch);
        }
        {
            var Q0;
            Q0 = qSketchRegion(id + "F16", true);
            var Q1;
            Q1=makeQuery(id+"F2.opExtrude","CAP_FACE",FACE,{"disambiguationData":[OSD([sQuery(id+"F0.wireOp",EDGE,"E12"),sQuery(id+"F0.wireOp",EDGE,"E13"),sQuery(id+"F0.wireOp",EDGE,"E14"),sQuery(id+"F0.wireOp",EDGE,"E15"),sQuery(id+"F0.wireOp",EDGE,"E17.filletArc"),sQuery(id+"F0.wireOp",EDGE,"E18.filletArc"),sQuery(id+"F0.wireOp",EDGE,"E19.filletArc"),sQuery(id+"F0.wireOp",EDGE,"E20.filletArc"),sQuery(id+"F0.wireOp",EDGE,"E25.0"),sQuery(id+"F0.wireOp",EDGE,"E25.1"),sQuery(id+"F0.wireOp",EDGE,"E25.2"),sQuery(id+"F0.wireOp",EDGE,"E25.3"),sQuery(id+"F0.wireOp",EDGE,"E25.4"),sQuery(id+"F0.wireOp",EDGE,"E25.5"),sQuery(id+"F0.wireOp",EDGE,"E25.6"),sQuery(id+"F0.wireOp",EDGE,"E25.7")])],"isStart":false});
            extrude(context, id + "F17", {"entities" : qUnion([Q0]), "endBound" : BoundingType.UP_TO_SURFACE, "depth" : 25 * mm, "endBoundEntityFace" : qUnion([Q1]), "offsetDistance" : 25 * mm});
        }
    });
